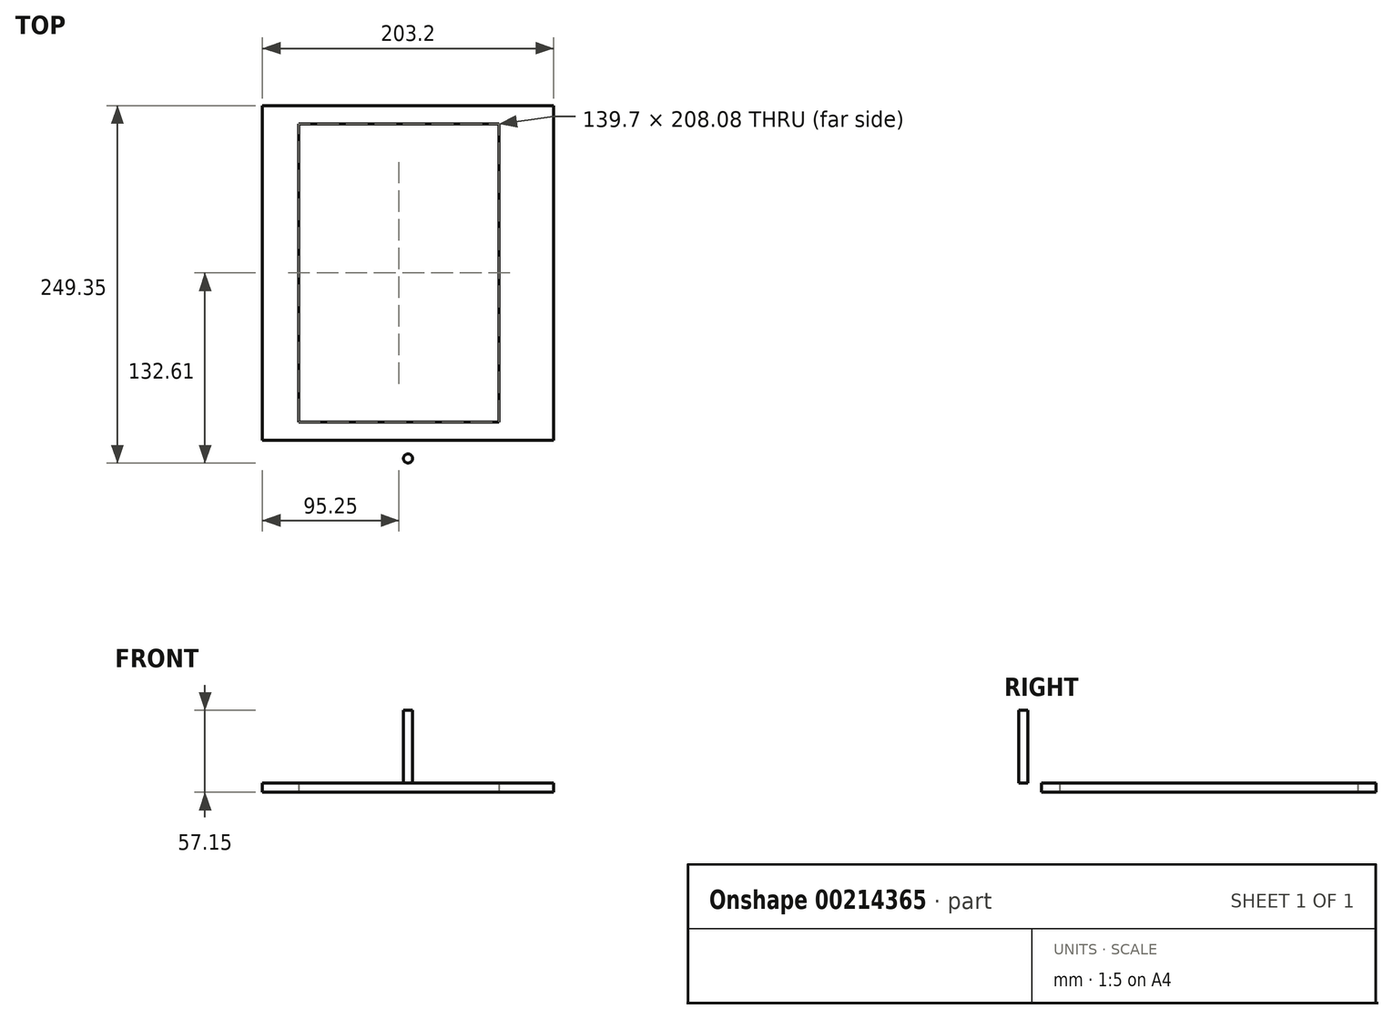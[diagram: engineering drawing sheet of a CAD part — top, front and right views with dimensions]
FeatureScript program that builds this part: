
annotation { "Feature Type Name" : "Feature", "Feature Type Description" : "" }
export const myFeature = defineFeature(function(context is Context, id is Id, definition is map)
    precondition{}
    {
        {
            var Q0;
            Q0=qCreatedBy(makeId("Top.planeOp"),FACE);
            var sketch = newSketch(context, id + "F0", { "sketchPlane" : qUnion([Q0])});
            skLineSegment(sketch, "E0.bottom", {"start": v(76.2, -91.34) * mm, "end": v(-76.2, -91.34) * mm});
            skLineSegment(sketch, "E0.top", {"start": v(76.2, 91.34) * mm, "end": v(-76.2, 91.34) * mm});
            skLineSegment(sketch, "E0.left", {"start": v(76.2, -91.34) * mm, "end": v(76.2, 91.34) * mm});
            skLineSegment(sketch, "E0.right", {"start": v(-76.2, -91.34) * mm, "end": v(-76.2, 91.34) * mm});
            skPoint(sketch, "E0.middle", {"position": v(0, 0) * mm});
            skLineSegment(sketch, "E1.0", {"start": v(101.6, 116.74) * mm, "end": v(-101.6, 116.74) * mm});
            skLineSegment(sketch, "E1.1", {"start": v(101.6, -116.74) * mm, "end": v(101.6, 116.74) * mm});
            skLineSegment(sketch, "E1.2", {"start": v(101.6, -116.74) * mm, "end": v(-101.6, -116.74) * mm});
            skLineSegment(sketch, "E1.3", {"start": v(-101.6, -116.74) * mm, "end": v(-101.6, 116.74) * mm});
            skLineSegment(sketch, "E2.bottom", {"start": v(-101.6, 116.74) * mm, "end": v(101.6, 116.74) * mm});
            skLineSegment(sketch, "E2.top", {"start": v(-101.6, 142.14) * mm, "end": v(101.6, 142.14) * mm});
            skLineSegment(sketch, "E2.left", {"start": v(-101.6, 116.74) * mm, "end": v(-101.6, 142.14) * mm});
            skLineSegment(sketch, "E2.right", {"start": v(101.6, 116.74) * mm, "end": v(101.6, 142.14) * mm});
            skLineSegment(sketch, "E3.bottom", {"start": v(-101.6, -116.74) * mm, "end": v(101.6, -116.74) * mm});
            skLineSegment(sketch, "E3.top", {"start": v(-101.6, -142.14) * mm, "end": v(101.6, -142.14) * mm});
            skLineSegment(sketch, "E3.left", {"start": v(-101.6, -116.74) * mm, "end": v(-101.6, -142.14) * mm});
            skLineSegment(sketch, "E3.right", {"start": v(101.6, -116.74) * mm, "end": v(101.6, -142.14) * mm});
            skLineSegment(sketch, "E4", {"start": v(101.6, 142.14) * mm, "end": v(127, 142.14) * mm});
            skLineSegment(sketch, "E5", {"start": v(127, 142.14) * mm, "end": v(127, -142.14) * mm});
            skLineSegment(sketch, "E6", {"start": v(127, -142.14) * mm, "end": v(101.6, -142.14) * mm});
            skLineSegment(sketch, "E7", {"start": v(76.2, -91.34) * mm, "end": v(76.2, -104.04) * mm});
            skLineSegment(sketch, "E8", {"start": v(76.2, -104.04) * mm, "end": v(-76.2, -104.04) * mm});
            skLineSegment(sketch, "E9", {"start": v(-76.2, -104.04) * mm, "end": v(-76.2, -91.34) * mm});
            skLineSegment(sketch, "E10", {"start": v(-63.5, 91.34) * mm, "end": v(-63.5, -104.04) * mm});
            skLineSegment(sketch, "E11", {"start": v(-76.2, 91.34) * mm, "end": v(-76.2, 104.04) * mm});
            skLineSegment(sketch, "E12", {"start": v(-76.2, 104.04) * mm, "end": v(76.2, 104.04) * mm});
            skLineSegment(sketch, "E13", {"start": v(76.2, 104.04) * mm, "end": v(76.2, 91.34) * mm});
            skLineSegment(sketch, "E14", {"start": v(-63.5, 91.34) * mm, "end": v(-63.5, 104.04) * mm});
            skLineSegment(sketch, "E15", {"start": v(63.5, 104.04) * mm, "end": v(63.5, -104.04) * mm});
            skSolve(sketch);
        }
        {
            var Q0;
            Q0=makeQuery(id+"F0.imprint","IMPRINT",FACE,{"disambiguationData":[TD([[makeQuery(id+"F0.imprint","IMPRINT",EDGE,{"derivedFrom":sQuery(id+"F0.wireOp",EDGE,"E2.bottom")}),1.0]])]});
            var Q1;
            Q1=makeQuery(id+"F0.imprint","IMPRINT",FACE,{"disambiguationData":[TD([[makeQuery(id+"F0.imprint","IMPRINT",EDGE,{"derivedFrom":sQuery(id+"F0.wireOp",EDGE,"E3.bottom")}),-1.0]])]});
            var Q2;
            Q2=makeQuery(id+"F0.imprint","IMPRINT",FACE,{"disambiguationData":[TD([[makeQuery(id+"F0.imprint","IMPRINT",EDGE,{"derivedFrom":sQuery(id+"F0.wireOp",EDGE,"E0.left")}),-1.0]])]});
            var Q3;
            {var subQ0=sQuery(id+"F0.wireOp",EDGE,"E0.left");Q3=makeQuery(id+"F0.imprint","IMPRINT",FACE,{"disambiguationData":[TD([[makeQuery(id+"F0.imprint","IMPRINT",EDGE,{"derivedFrom":subQ0}),1.0]])]});}
            var Q4;
            {var subQ0=sQuery(id+"F0.wireOp",EDGE,"E7");Q4=makeQuery(id+"F0.imprint","IMPRINT",FACE,{"disambiguationData":[TD([[makeQuery(id+"F0.imprint","IMPRINT",EDGE,{"derivedFrom":subQ0}),-1.0]])]});}
            var Q5;
            {var subQ0=sQuery(id+"F0.wireOp",EDGE,"E13");Q5=makeQuery(id+"F0.imprint","IMPRINT",FACE,{"disambiguationData":[TD([[makeQuery(id+"F0.imprint","IMPRINT",EDGE,{"derivedFrom":subQ0}),-1.0]])]});}
            extrude(context, id + "F1", {"entities" : qUnion([Q0, Q1, Q2, Q3, Q4, Q5]), "depth" : 6.35 * mm});
        }
        {
            var Q0;
            Q0=makeQuery(id+"F1.opExtrude","CAP_FACE",FACE,{"disambiguationData":[OSD([sQuery(id+"F0.wireOp",EDGE,"E0.right"),sQuery(id+"F0.wireOp",EDGE,"E1.1"),sQuery(id+"F0.wireOp",EDGE,"E1.3"),sQuery(id+"F0.wireOp",EDGE,"E2.top"),sQuery(id+"F0.wireOp",EDGE,"E2.left"),sQuery(id+"F0.wireOp",EDGE,"E2.right"),sQuery(id+"F0.wireOp",EDGE,"E3.top"),sQuery(id+"F0.wireOp",EDGE,"E3.left"),sQuery(id+"F0.wireOp",EDGE,"E3.right"),sQuery(id+"F0.wireOp",EDGE,"E8"),sQuery(id+"F0.wireOp",EDGE,"E9"),sQuery(id+"F0.wireOp",EDGE,"E11"),sQuery(id+"F0.wireOp",EDGE,"E12"),sQuery(id+"F0.wireOp",EDGE,"E15")])],"isStart":false});
            var sketch = newSketch(context, id + "F2", { "sketchPlane" : qUnion([Q0])});
            skCircle(sketch, "E16", {"center": v(0, -129.44) * mm, "radius": 3.18 * mm});
            skSolve(sketch);
        }
        {
            var Q0;
            Q0 = qSketchRegion(id + "F2", true);
            extrude(context, id + "F3", {"entities" : qUnion([Q0]), "operationType" : NewBodyOperationType.ADD, "depth" : 50.8 * mm});
        }
    });
